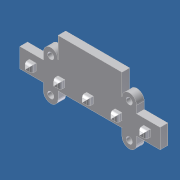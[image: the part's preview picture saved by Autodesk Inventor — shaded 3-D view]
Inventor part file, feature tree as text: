
AUTODESK INVENTOR PART (.ipt)
format: ipt  version: unknown  size: 444,928 bytes
history: native  units: in
note: dims shown in document units (in); Inventor stores cm internally (conversion verified against a paired STEP export)
features: extrude x6, sketch x6, chamfer x1, fillet x1
ambient origin geometry x8: Origin, YZ Plane, XZ Plane, XY Plane, X Axis, Y Axis, Z Axis, Center Point
feature tree (14):
  extrude  "Extrusion2"  Depth=0.2in TaperAngle=0.0deg
  extrude  "Extrusion3"  Depth=0.085in TaperAngle=45.0deg
  extrude  "Extrusion4"  Depth=0.2in TaperAngle=0.0deg
  chamfer  "Chamfer1"  Distance=1.0in
  fillet  "Fillet1"  Radius=0.7465in
  extrude  "Extrusion7"  [1 undecoded]
  extrude  "Extrusion8"  [1 undecoded]
  extrude  "Extrusion9"  [1 undecoded]
  sketch  "Sketch1"  dims[d14=0.2in d15=0.0in d16=0.2in d17=0.0in]
  sketch  "Sketch2"  dims[d18=0.2in d19=0.0in d20=0.085in d21=0.125in d22=45.0deg]
  sketch  "Sketch3"  dims[d23=0.125in d36=0.2in d37=0.0in d38=1.0in d39=0.0in d40=0.7465in d41=0.0in]
  sketch  "Sketch4"
  sketch  "Sketch6"
  sketch  "Sketch7"
note: 3 required parameter values undecoded (feature->parameter linkage not recoverable at this tier; creation-order binding heuristic only, values carry confidence <= 0.55)
